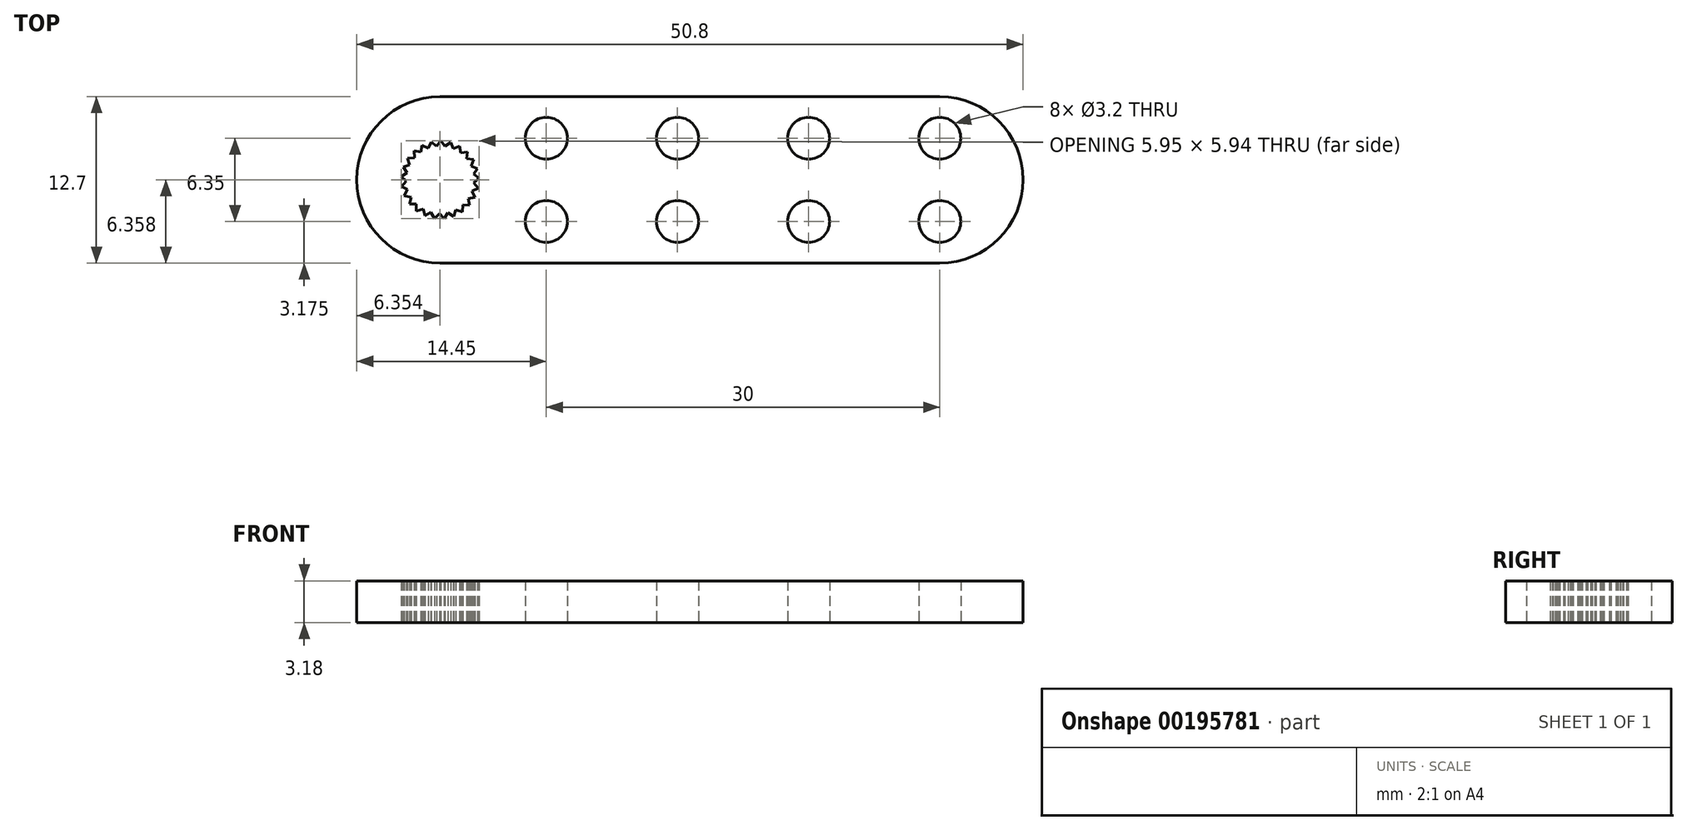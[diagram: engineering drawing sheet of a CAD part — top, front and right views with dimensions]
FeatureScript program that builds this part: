
annotation { "Feature Type Name" : "Feature", "Feature Type Description" : "" }
export const myFeature = defineFeature(function(context is Context, id is Id, definition is map)
    precondition{}
    {
        {
            var Q0;
            Q0=qCreatedBy(makeId("Top.planeOp"),FACE);
            var sketch = newSketch(context, id + "F0", { "sketchPlane" : qUnion([Q0])});
            skLineSegment(sketch, "E0", {"start": v(-2.48, 1.65) * mm, "end": v(-2.31, 1.15) * mm});
            skLineSegment(sketch, "E1", {"start": v(-2.31, 1.15) * mm, "end": v(-2.81, 0.98) * mm});
            skLineSegment(sketch, "E2.1.0", {"start": v(-2.81, 0.98) * mm, "end": v(-2.53, 0.54) * mm});
            skLineSegment(sketch, "E2.1.1", {"start": v(-2.53, 0.54) * mm, "end": v(-2.97, 0.25) * mm});
            skLineSegment(sketch, "E2.2.0", {"start": v(-2.97, 0.25) * mm, "end": v(-2.58, -0.1) * mm});
            skLineSegment(sketch, "E2.2.1", {"start": v(-2.58, -0.1) * mm, "end": v(-2.94, -0.5) * mm});
            skLineSegment(sketch, "E2.3.0", {"start": v(-2.94, -0.5) * mm, "end": v(-2.47, -0.74) * mm});
            skLineSegment(sketch, "E2.3.1", {"start": v(-2.47, -0.74) * mm, "end": v(-2.72, -1.2) * mm});
            skLineSegment(sketch, "E2.4.0", {"start": v(-2.72, -1.2) * mm, "end": v(-2.21, -1.34) * mm});
            skLineSegment(sketch, "E2.4.1", {"start": v(-2.21, -1.34) * mm, "end": v(-2.34, -1.85) * mm});
            skLineSegment(sketch, "E2.5.0", {"start": v(-2.34, -1.85) * mm, "end": v(-1.8, -1.84) * mm});
            skLineSegment(sketch, "E2.5.1", {"start": v(-1.8, -1.84) * mm, "end": v(-1.8, -2.37) * mm});
            skLineSegment(sketch, "E2.6.0", {"start": v(-1.8, -2.37) * mm, "end": v(-1.3, -2.24) * mm});
            skLineSegment(sketch, "E2.6.1", {"start": v(-1.3, -2.24) * mm, "end": v(-1.16, -2.75) * mm});
            skLineSegment(sketch, "E2.7.0", {"start": v(-1.16, -2.75) * mm, "end": v(-0.7, -2.49) * mm});
            skLineSegment(sketch, "E2.7.1", {"start": v(-0.7, -2.49) * mm, "end": v(-0.44, -2.95) * mm});
            skLineSegment(sketch, "E2.8.0", {"start": v(-0.44, -2.95) * mm, "end": v(-0.06, -2.58) * mm});
            skLineSegment(sketch, "E2.8.1", {"start": v(-0.06, -2.58) * mm, "end": v(0.3, -2.96) * mm});
            skLineSegment(sketch, "E2.9.0", {"start": v(0.3, -2.96) * mm, "end": v(0.59, -2.52) * mm});
            skLineSegment(sketch, "E2.9.1", {"start": v(0.59, -2.52) * mm, "end": v(1.04, -2.8) * mm});
            skLineSegment(sketch, "E2.10.0", {"start": v(1.04, -2.8) * mm, "end": v(1.2, -2.3) * mm});
            skLineSegment(sketch, "E2.10.1", {"start": v(1.2, -2.3) * mm, "end": v(1.7, -2.45) * mm});
            skLineSegment(sketch, "E2.11.0", {"start": v(1.7, -2.45) * mm, "end": v(1.73, -1.92) * mm});
            skLineSegment(sketch, "E2.11.1", {"start": v(1.73, -1.92) * mm, "end": v(2.25, -1.95) * mm});
            skLineSegment(sketch, "E2.12.0", {"start": v(2.25, -1.95) * mm, "end": v(2.15, -1.43) * mm});
            skLineSegment(sketch, "E2.12.1", {"start": v(2.15, -1.43) * mm, "end": v(2.67, -1.33) * mm});
            skLineSegment(sketch, "E2.13.0", {"start": v(2.67, -1.33) * mm, "end": v(2.44, -0.85) * mm});
            skLineSegment(sketch, "E2.13.1", {"start": v(2.44, -0.85) * mm, "end": v(2.91, -0.62) * mm});
            skLineSegment(sketch, "E2.14.0", {"start": v(2.91, -0.62) * mm, "end": v(2.57, -0.22) * mm});
            skLineSegment(sketch, "E2.14.1", {"start": v(2.57, -0.22) * mm, "end": v(2.98, 0.12) * mm});
            skLineSegment(sketch, "E2.15.0", {"start": v(2.98, 0.12) * mm, "end": v(2.55, 0.43) * mm});
            skLineSegment(sketch, "E2.15.1", {"start": v(2.55, 0.43) * mm, "end": v(2.85, 0.86) * mm});
            skLineSegment(sketch, "E2.16.0", {"start": v(2.85, 0.86) * mm, "end": v(2.36, 1.05) * mm});
            skLineSegment(sketch, "E2.16.1", {"start": v(2.36, 1.05) * mm, "end": v(2.55, 1.54) * mm});
            skLineSegment(sketch, "E2.17.0", {"start": v(2.55, 1.54) * mm, "end": v(2.03, 1.6) * mm});
            skLineSegment(sketch, "E2.17.1", {"start": v(2.03, 1.6) * mm, "end": v(2.09, 2.13) * mm});
            skLineSegment(sketch, "E2.18.0", {"start": v(2.09, 2.13) * mm, "end": v(1.56, 2.06) * mm});
            skLineSegment(sketch, "E2.18.1", {"start": v(1.56, 2.06) * mm, "end": v(1.5, 2.58) * mm});
            skLineSegment(sketch, "E2.19.0", {"start": v(1.5, 2.58) * mm, "end": v(1, 2.38) * mm});
            skLineSegment(sketch, "E2.19.1", {"start": v(1, 2.38) * mm, "end": v(0.8, 2.87) * mm});
            skLineSegment(sketch, "E2.20.0", {"start": v(0.8, 2.87) * mm, "end": v(0.38, 2.56) * mm});
            skLineSegment(sketch, "E2.20.1", {"start": v(0.38, 2.56) * mm, "end": v(0.07, 2.98) * mm});
            skLineSegment(sketch, "E2.21.0", {"start": v(0.07, 2.98) * mm, "end": v(-0.27, 2.57) * mm});
            skLineSegment(sketch, "E2.21.1", {"start": v(-0.27, 2.57) * mm, "end": v(-0.68, 2.9) * mm});
            skLineSegment(sketch, "E2.22.0", {"start": v(-0.68, 2.9) * mm, "end": v(-0.9, 2.42) * mm});
            skLineSegment(sketch, "E2.22.1", {"start": v(-0.9, 2.42) * mm, "end": v(-1.38, 2.64) * mm});
            skLineSegment(sketch, "E2.23.0", {"start": v(-1.38, 2.64) * mm, "end": v(-1.47, 2.12) * mm});
            skLineSegment(sketch, "E2.23.1", {"start": v(-1.47, 2.12) * mm, "end": v(-2, 2.22) * mm});
            skLineSegment(sketch, "E2.24.0", {"start": v(-2, 2.22) * mm, "end": v(-1.95, 1.69) * mm});
            skLineSegment(sketch, "E2.24.1", {"start": v(-1.95, 1.69) * mm, "end": v(-2.48, 1.65) * mm});
            skPoint(sketch, "E2.center", {"position": v(0, 0) * mm});
            skLineSegment(sketch, "E3.bottom", {"start": v(0, 6.35) * mm, "end": v(38.1, 6.35) * mm});
            skLineSegment(sketch, "E3.top", {"start": v(0, -6.35) * mm, "end": v(38.1, -6.35) * mm});
            skLineSegment(sketch, "E3.left", {"start": v(-6.35, 0) * mm, "end": v(-6.35, 0) * mm});
            skLineSegment(sketch, "E3.right", {"start": v(44.45, 0) * mm, "end": v(44.45, 0) * mm});
            skPoint(sketch, "E4.visualSharp", {"position": v(-6.35, 6.35) * mm});
            skArc(sketch, "E4.filletArc", {"start": v(0, 6.35) * mm, "mid": v(-4.5, 4.5) * mm, "end": v(-6.35, 0) * mm});
            skPoint(sketch, "E5.visualSharp", {"position": v(-6.35, -6.35) * mm});
            skArc(sketch, "E5.filletArc", {"start": v(-6.35, 0) * mm, "mid": v(-4.5, -4.5) * mm, "end": v(0, -6.35) * mm});
            skPoint(sketch, "E6.visualSharp", {"position": v(44.45, 6.35) * mm});
            skArc(sketch, "E6.filletArc", {"start": v(44.45, 0) * mm, "mid": v(42.6, 4.5) * mm, "end": v(38.1, 6.35) * mm});
            skPoint(sketch, "E7.visualSharp", {"position": v(44.45, -6.35) * mm});
            skArc(sketch, "E7.filletArc", {"start": v(38.1, -6.35) * mm, "mid": v(42.6, -4.5) * mm, "end": v(44.45, 0) * mm});
            skCircle(sketch, "E8", {"center": v(38.1, 3.18) * mm, "radius": 1.6 * mm});
            skCircle(sketch, "E9.1.0.0", {"center": v(28.1, 3.17) * mm, "radius": 1.6 * mm});
            skCircle(sketch, "E9.2.0.0", {"center": v(18.1, 3.17) * mm, "radius": 1.6 * mm});
            skCircle(sketch, "E10.0.3.0", {"center": v(8.1, 3.17) * mm, "radius": 1.6 * mm});
            skCircle(sketch, "E11.MirrorC", {"center": v(18.1, -3.17) * mm, "radius": 1.6 * mm});
            skCircle(sketch, "E12.MirrorC", {"center": v(8.1, -3.17) * mm, "radius": 1.6 * mm});
            skCircle(sketch, "E13.MirrorC", {"center": v(28.1, -3.17) * mm, "radius": 1.6 * mm});
            skCircle(sketch, "E14.MirrorC", {"center": v(38.1, -3.18) * mm, "radius": 1.6 * mm});
            skSolve(sketch);
        }
        {
            var Q0;
            Q0=makeQuery(id+"F0.imprint","IMPRINT",FACE,{"disambiguationData":[TD([[makeQuery(id+"F0.imprint","IMPRINT",EDGE,{"derivedFrom":sQuery(id+"F0.wireOp",EDGE,"E0")}),-1.0]])]});
            extrude(context, id + "F1", {"entities" : qUnion([Q0]), "depth" : 3.17 * mm});
        }
    });
